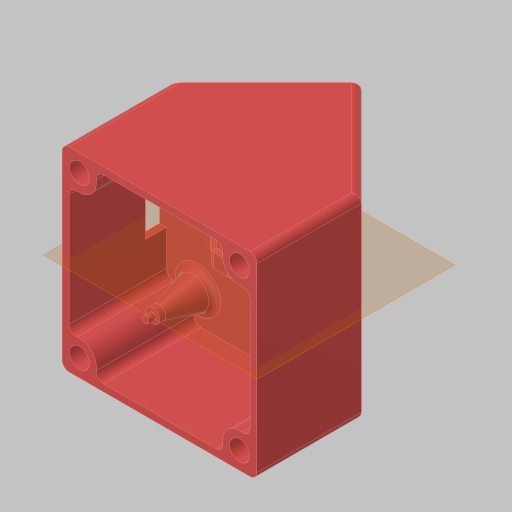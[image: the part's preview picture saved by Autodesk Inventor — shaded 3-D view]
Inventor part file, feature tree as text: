
AUTODESK INVENTOR PART (.ipt)
format: ipt  version: 2023.5 (Build 275446000, 446)  size: 364,032 bytes
history: native  units: in
note: dims shown in document units (in); Inventor stores cm internally (conversion verified against a paired STEP export)
features: extrude x7, projected_geometry x4, hole x2, fillet x2, chamfer x2, mirror x1, shell x1, plane x1, sketch x1
ambient origin geometry x8: Origin, YZ Plane, XZ Plane, XY Plane, X Axis, Y Axis, Z Axis, Center Point
bodies: Solid1 (feature_tree)
feature tree (21):
  extrude  "Extrusion1"  Depth=0.375in
  hole  "Hole1"  [1 undecoded]
  extrude  "Extrusion6"  Depth=0.375in
  mirror  "Mirror1"
  shell  "Shell1"  Thickness=1.1811in
  extrude  "Extrusion7"  Depth=0.0787in
  fillet  "Fillet1"  Radius=0.3937in
  extrude  "Extrusion2"  Depth=0.375in
  chamfer  "Chamfer1"  Distance=0.0787in
  extrude  "Extrusion3"  Depth=0.375in
  extrude  "Extrusion4"  Depth=0.375in
  plane  "Work Plane1"
  extrude  "Extrusion5"  Depth=0.375in
  chamfer  "Chamfer2"  Distance=0.1575in
  fillet  "Fillet3"  Radius=0.5906in
  hole  "Hole3"  [1 undecoded]
  projected_geometry  "Projected Loop1"
  projected_geometry  "Projected Loop2"
  projected_geometry  "Projected Loop3"
  sketch  "Sketch13"  dims[d0=1.4961in d1=1.4961in d2=1.3386in d3=1.3386in d5=1.1811in d6=0.0in d7=0.0787in d8=0.3937in d9=1.811in d10=0.2283in d11=0.2362in d12=0.385in d13=0.0787in d14=0.5635in d15=0.315in d16=0.8108in d17=0.0787in d18=0.1575in d19=0.1575in d20=0.1575in d21=0.1575in d22=0.5906in d23=0.0in d24=0.1181in d25=0.0787in d26=75.0deg d27=0.0748in d28=0.0748in d29=0.0748in d30=0.0748in d31=0.0787in d32=0.0in d33=0.4724in d34=0.2362in d35=0.0787in d36=1.1811in d37=0.0in d42=0.1969in d43=0.0in d44=0.0197in d45=0.0787in d46=0.481in d47=0.2283in d48=0.2283in d49=0.1969in d50=1.0in d51=0.2756in d52=0.0in d61=0.0787in d62=45.0deg d63=0.3937in d64=0.0in d65=0.0591in d66=0.1969in d67=0.5906in d68=45.0deg d69=45.0deg d70=0.5906in d71=0.1843in d72=0.0591in d73=0.0591in d87=0.3779in d88=1.25in d89=0.5in d90=0.5in d91=0.2657in d92=0.2362in d93=0.75in d94=0.188in d95=0.5635in d96=0.375in d97=0.0in d60=0.0in]
  projected_geometry  "Project Cut Edges1"
note: 2 required parameter values undecoded (feature->parameter linkage not recoverable at this tier; creation-order binding heuristic only, values carry confidence <= 0.55)
